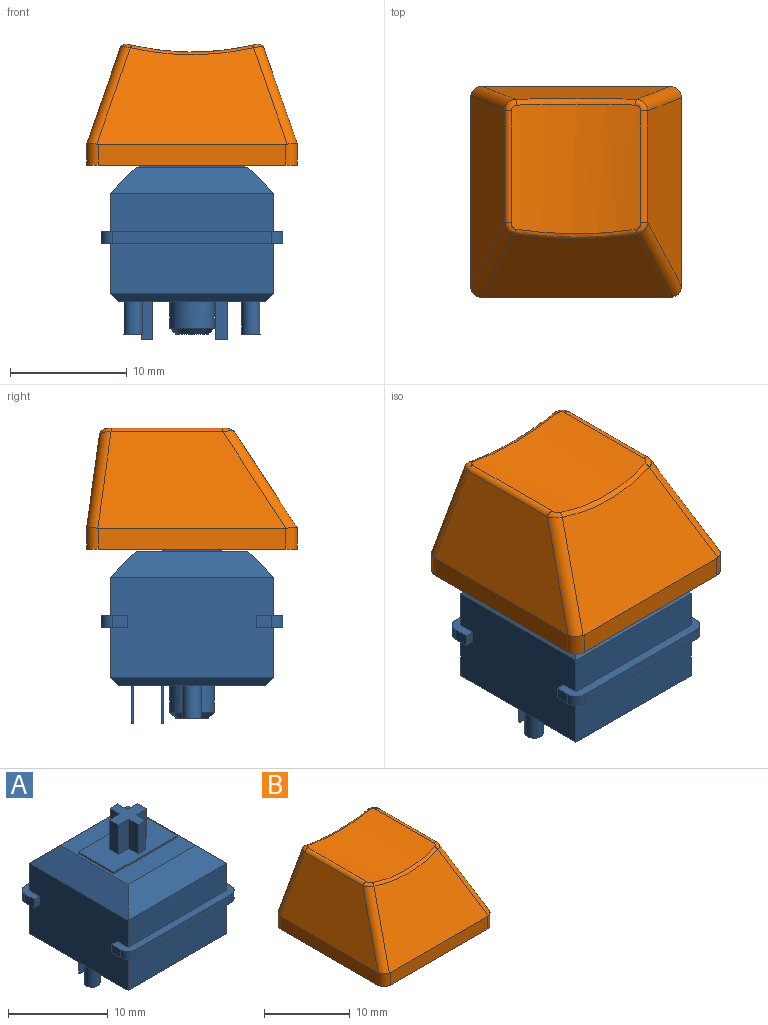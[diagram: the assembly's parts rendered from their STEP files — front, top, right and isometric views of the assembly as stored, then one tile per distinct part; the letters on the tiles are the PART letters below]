
ASSEMBLY  parts=2 mates=1
PART A: 69 faces, bbox 15.6x15.6x18.6 mm
  f0: plane 15.6x2.3mm, normal (0,0,-1), area 14.4mm2, adj f2,f3,f28,f30,f35,f60,f62,f63
  f1: plane 15.6x2.3mm, normal (0,0,-1), area 14.4mm2, adj f28,f30,f33,f34,f36,f59,f61,f64
  f2: plane 1.3x1mm, normal (1,0,0), area 1.3mm2, adj f0,f32,f62,f66
  f3: plane 1.3x1mm, normal (-1,0,0), area 1.3mm2, adj f0,f32,f63,f68
  f4: plane 15.6x2.3mm, normal (0,0,1), area 14.4mm2, adj f28,f30,f31,f33,f34,f36,f61,f64
  f5: plane 14x2.2mm, normal (-0.71,0,0.71), area 36.7mm2, adj f6,f7,f26,f30
  f6: plane 14x2.2mm, normal (0,-0.71,0.71), area 36.7mm2, adj f5,f7,f27,f31
  f7: plane 9.6x9.6mm, normal (0,0,1), area 47.2mm2, adj f5,f6,f8,f9,f10,f11,f26,f27
  f8: plane 5x0.2mm, normal (1,0,0), area 1mm2, adj f7,f9,f11,f12
  f9: plane 9x0.2mm, normal (0,1,0), area 1.8mm2, adj f7,f8,f10,f12
  f10: plane 5x0.2mm, normal (-1,0,0), area 1mm2, adj f7,f9,f11,f12
  f11: plane 9x0.2mm, normal (0,-1,0), area 1.8mm2, adj f7,f8,f10,f12
  f12: plane 9x5mm, normal (0,0,1), area 36.9mm2, adj f8,f9,f10,f11,f13,f14,f15,f16
  f13: plane 3.6x1.35mm, normal (1,0,0), area 4.9mm2, adj f12,f14,f24,f25
  f14: plane 3.6x1.08mm, normal (0,1,0), area 3.9mm2, adj f12,f13,f15,f25
  f15: plane 3.6x1.35mm, normal (-1,0,0), area 4.9mm2, adj f12,f14,f16,f25
  f16: plane 3.6x1.46mm, normal (0,1,0), area 5.3mm2, adj f12,f15,f17,f25
  f17: plane 3.6x1.3mm, normal (-1,0,0), area 4.7mm2, adj f12,f16,f18,f25
  f18: plane 3.6x1.46mm, normal (0,-1,0), area 5.3mm2, adj f12,f17,f19,f25
  f19: plane 3.6x1.35mm, normal (-1,0,0), area 4.9mm2, adj f12,f18,f20,f25
  f20: plane 3.6x1.08mm, normal (0,-1,0), area 3.9mm2, adj f12,f19,f21,f25
  f21: plane 3.6x1.35mm, normal (1,0,0), area 4.9mm2, adj f12,f20,f22,f25
  f22: plane 3.6x1.46mm, normal (0,-1,0), area 5.3mm2, adj f12,f21,f23,f25
  f23: plane 3.6x1.3mm, normal (1,0,0), area 4.7mm2, adj f12,f22,f24,f25
  f24: plane 3.6x1.46mm, normal (0,1,0), area 5.3mm2, adj f12,f13,f23,f25
  f25: plane 4x4mm, normal (0,0,1), area 8.1mm2, adj f13,f14,f15,f16,f17,f18,f19,f20
  f26: plane 14x2.2mm, normal (0,0.71,0.71), area 36.7mm2, adj f5,f7,f27,f29
  f27: plane 14x2.2mm, normal (0.71,0,0.71), area 36.7mm2, adj f6,f7,f26,f28
  f28: plane 14x8.6mm, normal (1,0,0), area 117.4mm2, adj f0,f1,f4,f27,f29,f31,f32,f55
  f29: plane 14x3.3mm, normal (0,1,0), area 46.2mm2, adj f26,f28,f30,f32
  f30: plane 14x8.6mm, normal (-1,0,0), area 117.4mm2, adj f0,f1,f4,f5,f29,f31,f32,f57
  f31: plane 14x3.3mm, normal (0,-1,0), area 46.2mm2, adj f4,f6,f28,f30
  f32: plane 15.6x2.3mm, normal (0,0,1), area 14.4mm2, adj f2,f3,f28,f29,f30,f35,f62,f63
  f33: plane 13.6x1mm, normal (0,-1,0), area 13.6mm2, adj f1,f4,f61,f64
  f34: plane 1.3x1mm, normal (1,0,0), area 1.3mm2, adj f1,f4,f61,f65
  f35: plane 13.6x1mm, normal (0,1,0), area 13.6mm2, adj f0,f32,f62,f63
  f36: plane 1.3x1mm, normal (-1,0,0), area 1.3mm2, adj f1,f4,f64,f67
  f37: plane 2.85x2.85mm, normal (0,0,-1), area 6.4mm2, adj f38
  f38: cone r=1.43mm half-angle=45deg, axis (0,0,1), area 7.4mm2, adj f37,f43
  f39: plane 1x0.2mm, normal (0,0,-1), area 0.2mm2, adj f44,f45,f46,f47
  f40: plane 1x0.2mm, normal (0,0,-1), area 0.2mm2, adj f48,f49,f50,f51
  f41: plane 1.6x1.6mm, normal (0,0,-1), area 2mm2, adj f52
  f42: plane 1.6x1.6mm, normal (0,0,-1), area 2mm2, adj f53
  f43: cylinder r=1.93mm len=3.85mm, axis (0,0,1), area 27.8mm2, adj f38,f54
  f44: plane 3.3x0.2mm, normal (-1,0,0), area 0.7mm2, adj f39,f45,f47,f54
  f45: plane 3.3x1mm, normal (0,1,0), area 3.3mm2, adj f39,f44,f46,f54
  f46: plane 3.3x0.2mm, normal (1,0,0), area 0.7mm2, adj f39,f45,f47,f54
  f47: plane 3.3x1mm, normal (0,-1,0), area 3.3mm2, adj f39,f44,f46,f54
  f48: plane 3.3x0.2mm, normal (-1,0,0), area 0.7mm2, adj f40,f49,f51,f54
  f49: plane 3.3x1mm, normal (0,1,0), area 3.3mm2, adj f40,f48,f50,f54
  f50: plane 3.3x0.2mm, normal (1,0,0), area 0.7mm2, adj f40,f49,f51,f54
  f51: plane 3.3x1mm, normal (0,-1,0), area 3.3mm2, adj f40,f48,f50,f54
  f52: cylinder r=0.8mm len=2.8mm, axis (0,0,1), area 14.1mm2, adj f41,f54
  f53: cylinder r=0.8mm len=2.8mm, axis (0,0,1), area 14.1mm2, adj f42,f54
  f54: plane 12.6x12.6mm, normal (0,0,-1), area 142.7mm2, adj f43,f44,f45,f46,f47,f48,f49,f50
  f55: plane 14x0.7mm, normal (0.71,0,-0.71), area 13.2mm2, adj f28,f54,f56,f58
  f56: plane 14x0.7mm, normal (0,0.71,-0.71), area 13.2mm2, adj f54,f55,f57,f60
  f57: plane 14x0.7mm, normal (-0.71,0,-0.71), area 13.2mm2, adj f30,f54,f56,f58
  f58: plane 14x0.7mm, normal (0,-0.71,-0.71), area 13.2mm2, adj f54,f55,f57,f59
  f59: plane 14x4.3mm, normal (0,-1,0), area 60.2mm2, adj f1,f28,f30,f58
  f60: plane 14x4.3mm, normal (0,1,0), area 60.2mm2, adj f0,f28,f30,f56
  f61: cylinder r=1mm len=1mm, axis (0,0,-1), area 1.6mm2, adj f1,f4,f33,f34
  f62: cylinder r=1mm len=1mm, axis (0,0,1), area 1.6mm2, adj f0,f2,f32,f35
  f63: cylinder r=1mm len=1mm, axis (0,0,-1), area 1.6mm2, adj f0,f3,f32,f35
  f64: cylinder r=1mm len=1mm, axis (0,0,1), area 1.6mm2, adj f1,f4,f33,f36
  f65: plane 1x0.8mm, normal (0,1,0), area 0.8mm2, adj f1,f4,f28,f34
  f66: plane 1x0.8mm, normal (0,-1,0), area 0.8mm2, adj f0,f2,f28,f32
  f67: plane 1x0.8mm, normal (0,1,0), area 0.8mm2, adj f1,f4,f30,f36
  f68: plane 1x0.8mm, normal (0,-1,0), area 0.8mm2, adj f0,f3,f30,f32
PART B: 50 faces, bbox 18.3x18.1x10.5 mm
  f0: plane 18.1x18.1mm, normal (0,0,-1), area 67.5mm2, adj f1,f2,f3,f4,f10,f12,f14,f16
  f1: plane 16.1x1.8mm, normal (1,0,0), area 29mm2, adj f0,f8,f10,f16
  f2: plane 16.1x1.8mm, normal (0,1,0), area 29mm2, adj f0,f5,f14,f15,f16,f17
  f3: plane 16.1x1.8mm, normal (-1,0,0), area 29mm2, adj f0,f6,f12,f14
  f4: plane 16.1x1.8mm, normal (0,-1,0), area 29mm2, adj f0,f7,f10,f12
  f5: plane 16.08x8.06mm, normal (0,0.99,0.14), area 103.6mm2, adj f2,f15,f17,f20
  f6: plane 16.16x8.27mm, normal (-0.94,0,0.33), area 112.8mm2, adj f3,f12,f13,f14,f15,f19
  f7: plane 16.36x8.28mm, normal (0,-0.84,0.55), area 128.1mm2, adj f4,f10,f11,f12,f13,f23
  f8: plane 16.16x8.27mm, normal (0.94,0,0.33), area 112.8mm2, adj f1,f10,f11,f16,f17,f24
  f9: cylinder r=22.9mm len=11.13mm, axis (0,-1,0), area 122.7mm2, adj f18,f19,f20,f21,f22,f23,f24,f25
  f10: cylinder r=1mm len=1.87mm, axis (0,0,-1), area 2.9mm2, adj f0,f1,f4,f7,f8,f11
  f11: cylinder r=1mm len=8.74mm, axis (0.28,-0.53,-0.8), area 14.3mm2, adj f7,f8,f10,f25
  f12: cylinder r=1mm len=1.87mm, axis (0,0,1), area 2.9mm2, adj f0,f3,f4,f6,f7,f13
  f13: cylinder r=1mm len=8.74mm, axis (0.28,0.53,0.8), area 14.3mm2, adj f6,f7,f12,f21
  f14: cylinder r=1mm len=1.83mm, axis (0,0,-1), area 2.9mm2, adj f0,f2,f3,f6,f15
  f15: cylinder r=1mm len=8.48mm, axis (-0.33,0.13,-0.94), area 13.4mm2, adj f2,f5,f6,f14,f18
  f16: cylinder r=1mm len=1.83mm, axis (0,0,1), area 2.9mm2, adj f0,f1,f2,f8,f17
  f17: cylinder r=1mm len=8.48mm, axis (-0.33,-0.13,0.94), area 13.4mm2, adj f2,f5,f8,f16,f22
  f18: bspline ~1.24x1.22mm, area 0.9mm2, adj f9,f15,f19,f20
  f19: cylinder r=0.5mm len=9.6mm, axis (0,-1,0), area 7.1mm2, adj f6,f9,f18,f21
  f20: bspline ~10.43x1.01mm, area 7.4mm2, adj f5,f9,f18,f22
  f21: bspline ~1.28x1.11mm, area 0.7mm2, adj f9,f13,f19,f23
  f22: bspline ~1.22x1.09mm, area 0.9mm2, adj f9,f17,f20,f24
  f23: bspline ~10.56x0.82mm, area 5.3mm2, adj f7,f9,f21,f25
  f24: cylinder r=0.5mm len=9.6mm, axis (0,-1,0), area 7.1mm2, adj f8,f9,f22,f25
  f25: bspline ~1.28x1.11mm, area 0.7mm2, adj f9,f11,f23,f24
  f26: plane 16.1x1.63mm, normal (-1,0,0), area 26.2mm2, adj f0,f27,f29,f32,f33
  f27: plane 16.1x1.73mm, normal (0,-1,0), area 27.9mm2, adj f0,f26,f28,f30,f31,f33
  f28: plane 16.1x1.63mm, normal (1,0,0), area 26.2mm2, adj f0,f27,f29,f31,f32
  f29: plane 16.1x1.5mm, normal (0,1,0), area 24.2mm2, adj f0,f26,f28,f32
  f30: plane 16.03x7.58mm, normal (0,-0.99,-0.14), area 97.9mm2, adj f27,f31,f33,f34
  f31: plane 16.02x7.68mm, normal (0.94,0,-0.33), area 105.7mm2, adj f27,f28,f30,f32,f34
  f32: plane 16.1x7.81mm, normal (0,0.84,-0.55), area 120.3mm2, adj f26,f28,f29,f31,f33,f34
  f33: plane 16.02x7.68mm, normal (-0.94,0,-0.33), area 105.7mm2, adj f26,f27,f30,f32,f34
  f34: cylinder r=23.9mm len=10.72mm, axis (0,-1,0), area 87.1mm2, adj f30,f31,f32,f33,f46
  f35: plane 8.71x1.35mm, normal (-1,0,0), area 11.8mm2, adj f36,f44,f45,f49
  f36: plane 8.78x1.5mm, normal (0,-1,0), area 13.1mm2, adj f35,f37,f45,f49
  f37: plane 8.78x1.3mm, normal (-1,0,0), area 11.4mm2, adj f36,f38,f45,f49
  f38: plane 8.78x1.5mm, normal (0,1,0), area 13.1mm2, adj f37,f39,f45,f49
  f39: plane 8.71x1.35mm, normal (-1,0,0), area 11.8mm2, adj f38,f40,f45,f49
  f40: plane 8.71x1mm, normal (0,1,0), area 8.7mm2, adj f39,f41,f45,f49
  f41: plane 8.71x1.35mm, normal (1,0,0), area 11.8mm2, adj f40,f42,f45,f49
  f42: plane 8.78x1.5mm, normal (0,1,0), area 13.1mm2, adj f41,f43,f45,f49
  f43: plane 8.78x1.3mm, normal (1,0,0), area 11.4mm2, adj f42,f45,f47,f49
  f44: plane 8.71x1mm, normal (0,-1,0), area 8.7mm2, adj f35,f45,f48,f49
  f45: plane 5.5x5.5mm, normal (0,0,-1), area 15.9mm2, adj f35,f36,f37,f38,f39,f40,f41,f42
  f46: cylinder r=2.75mm len=8.86mm, axis (0,0,-1), area 151.7mm2, adj f34,f45
  f47: plane 8.78x1.5mm, normal (0,-1,0), area 13.1mm2, adj f43,f45,f48,f49
  f48: plane 8.71x1.35mm, normal (1,0,0), area 11.8mm2, adj f44,f45,f47,f49
  f49: cylinder r=23.9mm len=4mm, axis (0,-1,0), area 7.9mm2, adj f35,f36,f37,f38,f39,f40,f41,f42
PLACE A at identity fixed
PLACE B t=(0,0,11.7)mm
MATE fastened B.f46 <-> A.f38  axis (0,0,-1) through (0,0,11.7)mm
